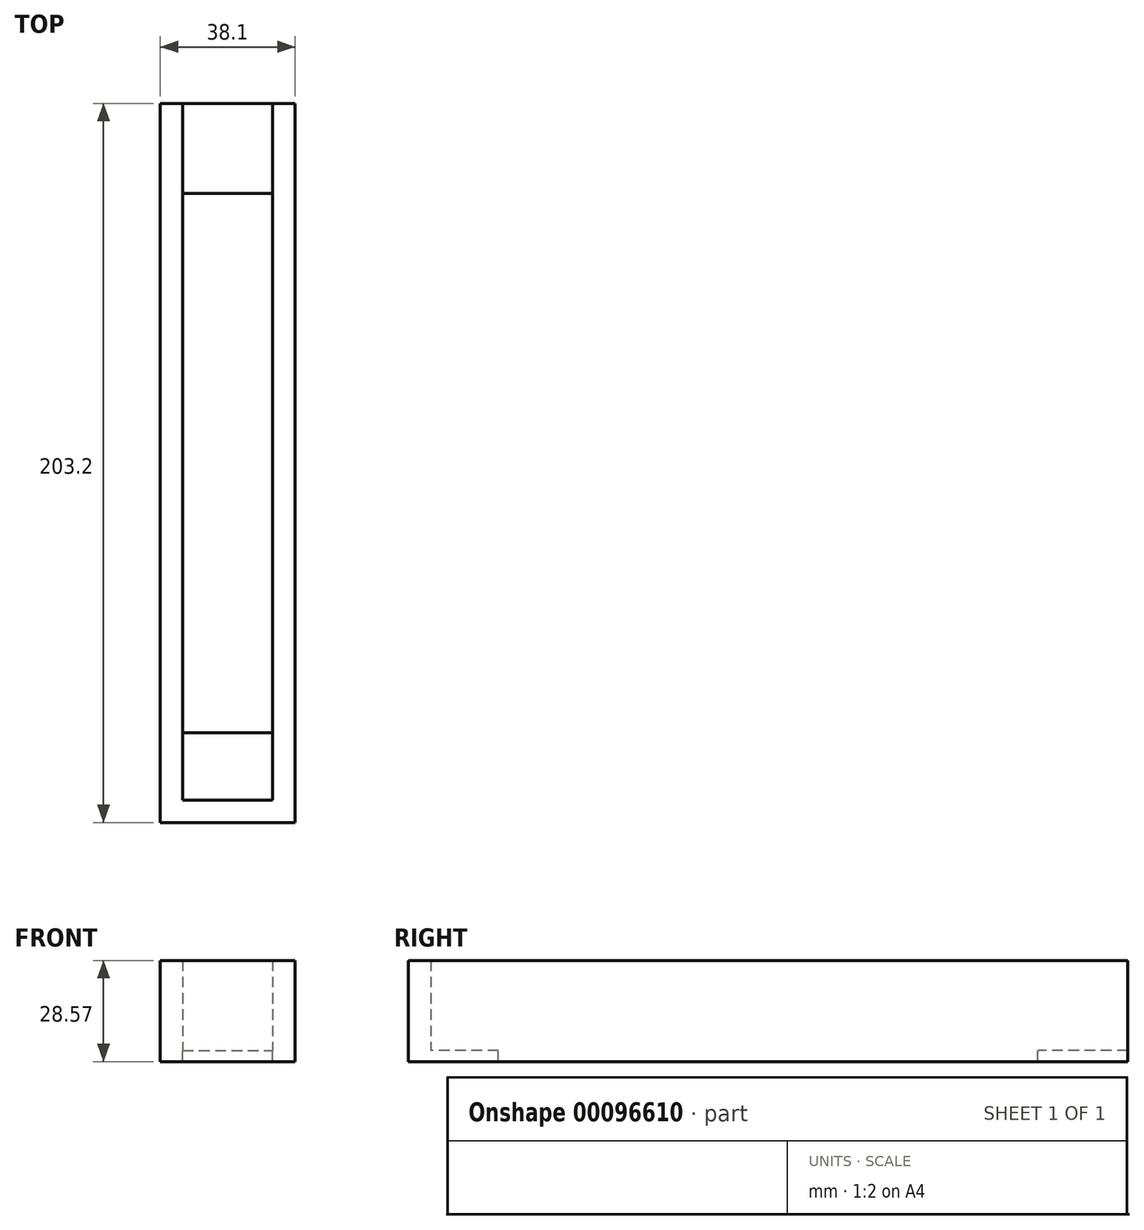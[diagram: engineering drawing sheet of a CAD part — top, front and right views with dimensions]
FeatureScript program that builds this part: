
annotation { "Feature Type Name" : "Feature", "Feature Type Description" : "" }
export const myFeature = defineFeature(function(context is Context, id is Id, definition is map)
    precondition{}
    {
        {
            var Q0;
            Q0=qCreatedBy(makeId("Top.planeOp"),FACE);
            var sketch = newSketch(context, id + "F0", { "sketchPlane" : qUnion([Q0])});
            skLineSegment(sketch, "E0.bottom", {"start": v(19.05, -101.6) * mm, "end": v(-19.05, -101.6) * mm});
            skLineSegment(sketch, "E0.top", {"start": v(19.05, 101.6) * mm, "end": v(-19.05, 101.6) * mm});
            skLineSegment(sketch, "E0.left", {"start": v(19.05, -101.6) * mm, "end": v(19.05, 101.6) * mm});
            skLineSegment(sketch, "E0.right", {"start": v(-19.05, -101.6) * mm, "end": v(-19.05, 101.6) * mm});
            skPoint(sketch, "E0.middle", {"position": v(0, 0) * mm});
            skSolve(sketch);
        }
        {
            var Q0;
            Q0 = qSketchRegion(id + "F0", true);
            extrude(context, id + "F1", {"entities" : qUnion([Q0]), "depth" : 3.17 * mm});
        }
        {
            var Q0;
            Q0=makeQuery(id+"F1.opExtrude","CAP_FACE",FACE,{"disambiguationData":[OSD([sQuery(id+"F0.wireOp",EDGE,"E0.bottom"),sQuery(id+"F0.wireOp",EDGE,"E0.top"),sQuery(id+"F0.wireOp",EDGE,"E0.left"),sQuery(id+"F0.wireOp",EDGE,"E0.right")])],"isStart":false});
            var sketch = newSketch(context, id + "F2", { "sketchPlane" : qUnion([Q0])});
            skLineSegment(sketch, "E1.bottom", {"start": v(-19.05, 101.6) * mm, "end": v(-12.7, 101.6) * mm});
            skLineSegment(sketch, "E1.top", {"start": v(-19.05, -101.6) * mm, "end": v(-12.7, -101.6) * mm});
            skLineSegment(sketch, "E1.left", {"start": v(-19.05, 101.6) * mm, "end": v(-19.05, -101.6) * mm});
            skLineSegment(sketch, "E1.right", {"start": v(-12.7, 101.6) * mm, "end": v(-12.7, -101.6) * mm});
            skLineSegment(sketch, "E2.bottom", {"start": v(19.05, 101.6) * mm, "end": v(12.7, 101.6) * mm});
            skLineSegment(sketch, "E2.top", {"start": v(19.05, -101.6) * mm, "end": v(12.7, -101.6) * mm});
            skLineSegment(sketch, "E2.left", {"start": v(19.05, 101.6) * mm, "end": v(19.05, -101.6) * mm});
            skLineSegment(sketch, "E2.right", {"start": v(12.7, 101.6) * mm, "end": v(12.7, -101.6) * mm});
            skLineSegment(sketch, "E3.bottom", {"start": v(-19.05, -101.6) * mm, "end": v(19.05, -101.6) * mm});
            skLineSegment(sketch, "E3.top", {"start": v(-19.05, -95.25) * mm, "end": v(19.05, -95.25) * mm});
            skLineSegment(sketch, "E3.left", {"start": v(-19.05, -101.6) * mm, "end": v(-19.05, -95.25) * mm});
            skLineSegment(sketch, "E3.right", {"start": v(19.05, -101.6) * mm, "end": v(19.05, -95.25) * mm});
            skSolve(sketch);
        }
        {
            var Q0;
            Q0 = qSketchRegion(id + "F2", true);
            extrude(context, id + "F3", {"entities" : qUnion([Q0]), "operationType" : NewBodyOperationType.ADD, "depth" : 25.4 * mm});
        }
        {
            var Q0;
            Q0=makeQuery(id+"F1.opExtrude","CAP_FACE",FACE,{"disambiguationData":[OSD([sQuery(id+"F0.wireOp",EDGE,"E0.bottom"),sQuery(id+"F0.wireOp",EDGE,"E0.top"),sQuery(id+"F0.wireOp",EDGE,"E0.left"),sQuery(id+"F0.wireOp",EDGE,"E0.right")])],"isStart":false});
            var sketch = newSketch(context, id + "F4", { "sketchPlane" : qUnion([Q0])});
            skLineSegment(sketch, "E4.bottom", {"start": v(-12.7, 76.2) * mm, "end": v(12.7, 76.2) * mm});
            skLineSegment(sketch, "E4.top", {"start": v(-12.7, -76.2) * mm, "end": v(12.7, -76.2) * mm});
            skLineSegment(sketch, "E4.left", {"start": v(-12.7, 76.2) * mm, "end": v(-12.7, -76.2) * mm});
            skLineSegment(sketch, "E4.right", {"start": v(12.7, 76.2) * mm, "end": v(12.7, -76.2) * mm});
            skPoint(sketch, "E4.middle", {"position": v(0, 0) * mm});
            skSolve(sketch);
        }
        {
            var Q0;
            Q0 = qSketchRegion(id + "F4", true);
            extrude(context, id + "F5", {"entities" : qUnion([Q0]), "operationType" : NewBodyOperationType.REMOVE, "endBound" : BoundingType.THROUGH_ALL, "oppositeDirection" : true, "depth" : 25.4 * mm});
        }
    });
